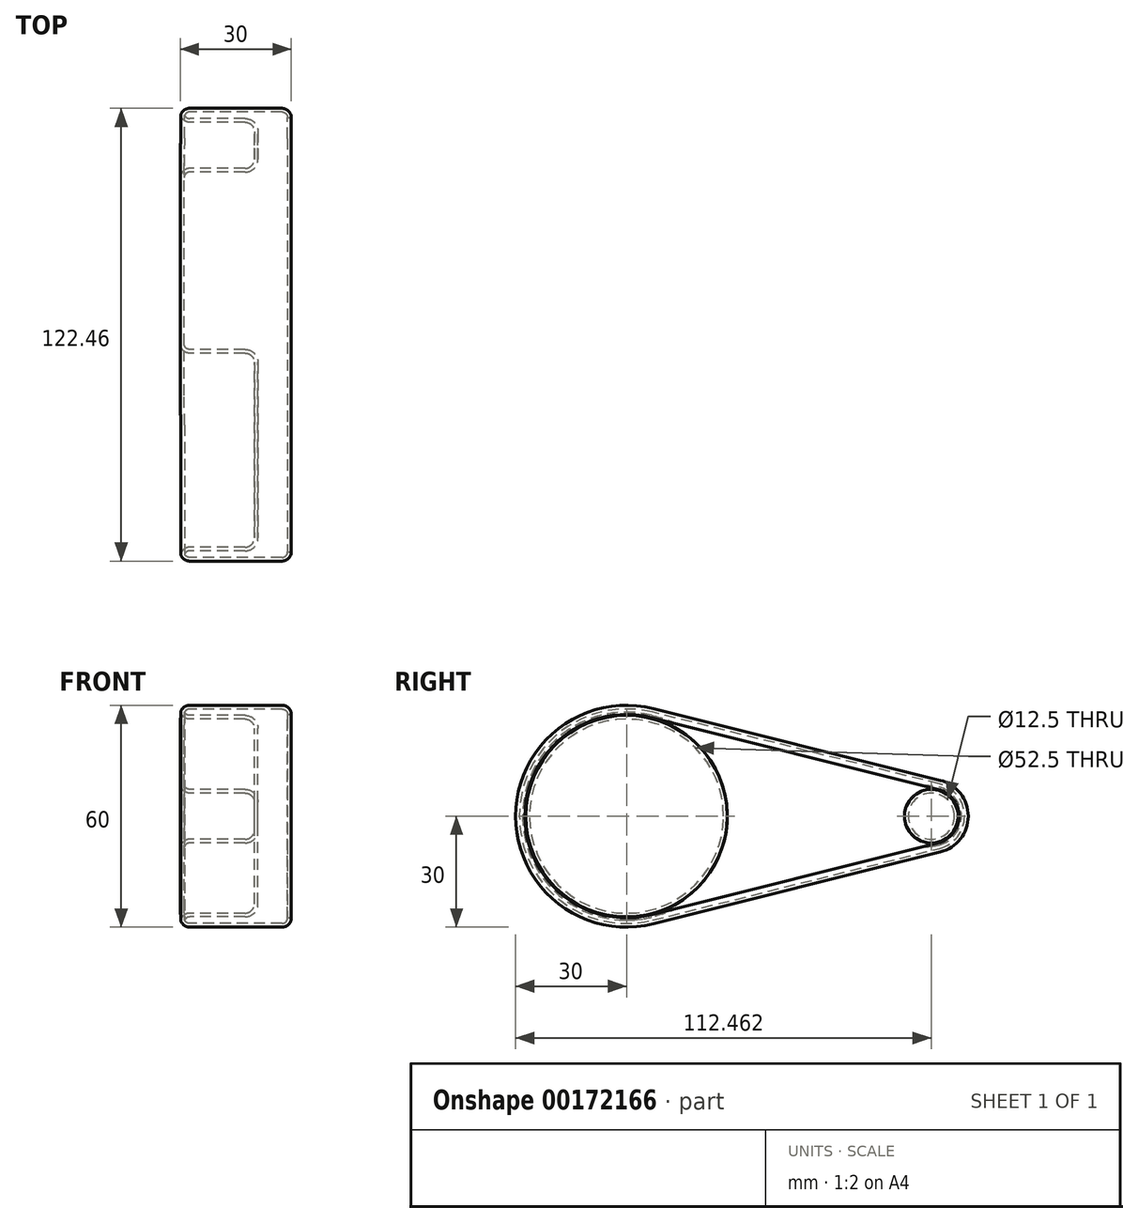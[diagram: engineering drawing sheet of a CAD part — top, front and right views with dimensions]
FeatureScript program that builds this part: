
annotation { "Feature Type Name" : "Feature", "Feature Type Description" : "" }
export const myFeature = defineFeature(function(context is Context, id is Id, definition is map)
    precondition{}
    {
        {
            var Q0;
            Q0=qCreatedBy(makeId("Right.planeOp"),FACE);
            var sketch = newSketch(context, id + "F0", { "sketchPlane" : qUnion([Q0])});
            skCircle(sketch, "E0", {"center": v(0, 0) * mm, "radius": 30 * mm});
            skCircle(sketch, "E1", {"center": v(82.46, 0) * mm, "radius": 10 * mm});
            skLineSegment(sketch, "E2", {"start": v(7.28, 29.1) * mm, "end": v(84.89, 9.7) * mm});
            skLineSegment(sketch, "E3", {"start": v(84.89, -9.7) * mm, "end": v(7.28, -29.1) * mm});
            skSolve(sketch);
        }
        {
            var Q0;
            {var subQ0=sQuery(id+"F0.wireOp",EDGE,"E0");var subQ1=makeQuery(id+"F0.imprint","INTERSECT",VERTEX,{"derivedFrom":[subQ0,sQuery(id+"F0.wireOp",EDGE,"E2")]});Q0=makeQuery(id+"F0.imprint","IMPRINT",FACE,{"disambiguationData":[TD([[makeQuery(id+"F0.imprint","IMPRINT",EDGE,{"disambiguationData":[TD([[subQ1,-1.0]])],"derivedFrom":subQ0}),1.0]])]});}
            var Q1;
            {var subQ0=sQuery(id+"F0.wireOp",EDGE,"E2");Q1=makeQuery(id+"F0.imprint","IMPRINT",FACE,{"disambiguationData":[TD([[makeQuery(id+"F0.imprint","IMPRINT",EDGE,{"derivedFrom":subQ0}),-1.0]])]});}
            var Q2;
            {var subQ0=sQuery(id+"F0.wireOp",EDGE,"E1");var subQ1=makeQuery(id+"F0.imprint","INTERSECT",VERTEX,{"derivedFrom":[subQ0,sQuery(id+"F0.wireOp",EDGE,"E2")]});Q2=makeQuery(id+"F0.imprint","IMPRINT",FACE,{"disambiguationData":[TD([[makeQuery(id+"F0.imprint","IMPRINT",EDGE,{"disambiguationData":[TD([[subQ1,-1.0]])],"derivedFrom":subQ0}),1.0]])]});}
            extrude(context, id + "F1", {"entities" : qUnion([Q0, Q1, Q2]), "depth" : 30 * mm});
        }
        {
            var Q0;
            Q0=qCreatedBy(makeId("Right.planeOp"),FACE);
            var sketch = newSketch(context, id + "F2", { "sketchPlane" : qUnion([Q0])});
            skCircle(sketch, "E4", {"center": v(0, 0) * mm, "radius": 26.25 * mm});
            skCircle(sketch, "E5", {"center": v(82.46, 0) * mm, "radius": 6.25 * mm});
            skSolve(sketch);
        }
        {
            var Q0;
            Q0=makeQuery(id+"F2.imprint","IMPRINT",FACE,{"disambiguationData":[TD([[makeQuery(id+"F2.imprint","IMPRINT",EDGE,{"derivedFrom":sQuery(id+"F2.wireOp",EDGE,"E4")}),1.0]])]});
            var Q1;
            Q1=makeQuery(id+"F2.imprint","IMPRINT",FACE,{"disambiguationData":[TD([[makeQuery(id+"F2.imprint","IMPRINT",EDGE,{"derivedFrom":sQuery(id+"F2.wireOp",EDGE,"E5")}),1.0]])]});
            extrude(context, id + "F3", {"entities" : qUnion([Q0, Q1]), "operationType" : NewBodyOperationType.REMOVE, "depth" : 20 * mm});
        }
        {
            var Q0;
            Q0=makeQuery(id+"F1.opExtrude","CAP_FACE",FACE,{"disambiguationData":[OSD([sQuery(id+"F0.wireOp",EDGE,"E0"),sQuery(id+"F0.wireOp",EDGE,"E1"),sQuery(id+"F0.wireOp",EDGE,"E2"),sQuery(id+"F0.wireOp",EDGE,"E3")])],"isStart":true});
            var Q1;
            Q1=makeQuery(id+"F1.opExtrude","CAP_FACE",FACE,{"disambiguationData":[OSD([sQuery(id+"F0.wireOp",EDGE,"E0"),sQuery(id+"F0.wireOp",EDGE,"E1"),sQuery(id+"F0.wireOp",EDGE,"E2"),sQuery(id+"F0.wireOp",EDGE,"E3")])],"isStart":false});
            var Q2;
            Q2=makeQuery(id+"F3.boolean.opBoolean","COPY",FACE,{"derivedFrom":makeQuery(id+"F3.opExtrude","CAP_FACE",FACE,{"disambiguationData":[OSD([sQuery(id+"F2.wireOp",EDGE,"E4")])],"isStart":false})});
            var Q3;
            Q3=makeQuery(id+"F3.boolean.opBoolean","COPY",FACE,{"derivedFrom":makeQuery(id+"F3.opExtrude","CAP_FACE",FACE,{"disambiguationData":[OSD([sQuery(id+"F2.wireOp",EDGE,"E5")])],"isStart":false})});
            fillet(context, id + "F4", {"entities" : qUnion([Q0, Q1, Q2, Q3]), "radius" : 2.5 * mm, "tangentPropagation" : true, "allowEdgeOverflow" : false});
        }
        {
            var Q0;
            Q0=makeQuery(id+"F1.opExtrude","CAP_FACE",FACE,{"disambiguationData":[OSD([sQuery(id+"F0.wireOp",EDGE,"E0"),sQuery(id+"F0.wireOp",EDGE,"E1"),sQuery(id+"F0.wireOp",EDGE,"E2"),sQuery(id+"F0.wireOp",EDGE,"E3")])],"isStart":false});
            shell(context, id + "F5", {"entities" : qUnion([Q0]), "thickness" : 1 * mm});
        }
    });
